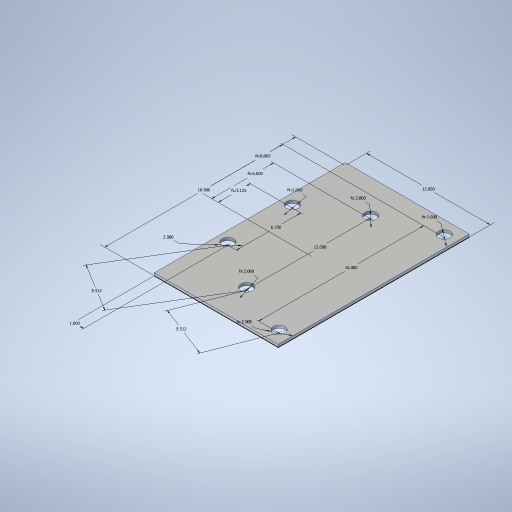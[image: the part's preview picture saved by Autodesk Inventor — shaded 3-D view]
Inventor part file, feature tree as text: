
AUTODESK INVENTOR PART (.ipt)
format: ipt  version: 2023.4 (Build 274418000, 418)  size: 259,584 bytes
history: native  units: in
note: dims shown in document units (in); Inventor stores cm internally (conversion verified against a paired STEP export)
features: sketch x1, extrude x1, hole x1
ambient origin geometry x8: Origin, YZ Plane, XZ Plane, XY Plane, X Axis, Y Axis, Z Axis, Center Point
bodies: Solid1 (feature_tree)
feature tree (3):
  sketch  "Sketch1"  dims[d0=12.0in d1=18.5in d2=6.25in d3=2.0in d4=2.0in d5=3.125in d6=2.0in d7=2.0in d8=2.0in d9=2.0in d10=16.0in d11=12.0in d12=6.0in d14=8.0in d17=5.512in d18=5.512in d19=1.0in d20=0.25in d21=0.0in d22=1.125in d23=0.75in d24=0.375in d25=0.25in d26=0.5635in d27=1.0in d28=0.8108in]
  extrude  "Extrusion1"  Depth=18.5in
  hole  "Hole1"  [1 undecoded]
note: 1 required parameter value undecoded (feature->parameter linkage not recoverable at this tier; creation-order binding heuristic only, values carry confidence <= 0.55)
